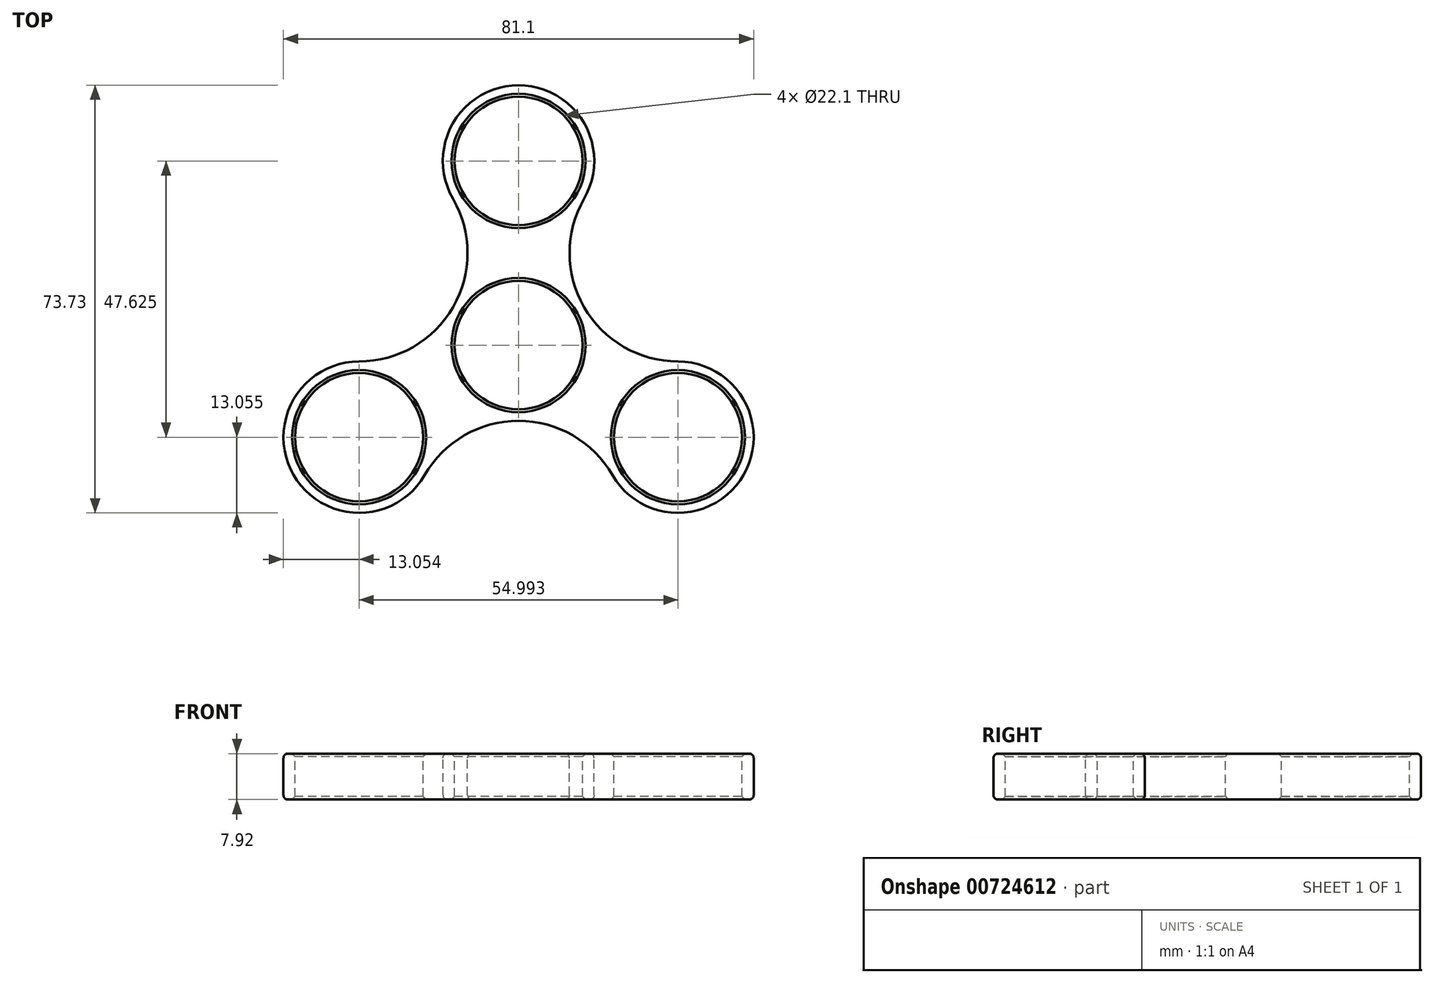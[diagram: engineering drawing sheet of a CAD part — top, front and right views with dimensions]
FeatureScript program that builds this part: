
annotation { "Feature Type Name" : "Feature", "Feature Type Description" : "" }
export const myFeature = defineFeature(function(context is Context, id is Id, definition is map)
    precondition{}
    {
        {
            var Q0;
            Q0=qCreatedBy(makeId("Top.planeOp"),FACE);
            var sketch = newSketch(context, id + "F0", { "sketchPlane" : qUnion([Q0])});
            skCircle(sketch, "E0", {"center": v(0, 0) * mm, "radius": 11.05 * mm});
            skCircle(sketch, "E1", {"center": v(0, 31.75) * mm, "radius": 11.05 * mm});
            skArc(sketch, "E2", {"start": v(11.3, 25.23) * mm, "mid": v(0, 44.8) * mm, "end": v(-11.3, 25.23) * mm});
            skCircle(sketch, "E3.1.0", {"center": v(-27.5, -15.87) * mm, "radius": 11.05 * mm});
            skArc(sketch, "E3.1.1", {"start": v(-27.5, -2.82) * mm, "mid": v(-38.8, -22.4) * mm, "end": v(-16.2, -22.4) * mm});
            skCircle(sketch, "E3.2.0", {"center": v(27.5, -15.88) * mm, "radius": 11.05 * mm});
            skArc(sketch, "E3.2.1", {"start": v(16.2, -22.4) * mm, "mid": v(38.8, -22.4) * mm, "end": v(27.5, -2.83) * mm});
            skArc(sketch, "E4", {"start": v(11.3, 25.22) * mm, "mid": v(11.3, 6.53) * mm, "end": v(27.5, -2.83) * mm});
            skArc(sketch, "E5.1.0", {"start": v(-27.5, -2.82) * mm, "mid": v(-11.3, 6.52) * mm, "end": v(-11.3, 25.22) * mm});
            skArc(sketch, "E5.2.0", {"start": v(16.2, -22.4) * mm, "mid": v(0, -13.05) * mm, "end": v(-16.2, -22.4) * mm});
            skSolve(sketch);
        }
        {
            var Q0;
            Q0 = qSketchRegion(id + "F0", true);
            extrude(context, id + "F1", {"entities" : qUnion([Q0]), "oppositeDirection" : true, "depth" : 7.92 * mm, "offsetDistance" : 25.4 * mm});
        }
        {
            var Q0;
            Q0=makeQuery(id+"F1.opExtrude","CAP_EDGE",EDGE,{"disambiguationData":[OSD([sQuery(id+"F0.wireOp",EDGE,"E3.2.0")])],"isStart":false});
            var Q1;
            Q1=makeQuery(id+"F1.opExtrude","CAP_EDGE",EDGE,{"disambiguationData":[OSD([sQuery(id+"F0.wireOp",EDGE,"E3.2.0")])],"isStart":true});
            var Q2;
            Q2=makeQuery(id+"F1.opExtrude","CAP_EDGE",EDGE,{"disambiguationData":[OSD([sQuery(id+"F0.wireOp",EDGE,"E3.1.0")])],"isStart":false});
            var Q3;
            Q3=makeQuery(id+"F1.opExtrude","CAP_EDGE",EDGE,{"disambiguationData":[OSD([sQuery(id+"F0.wireOp",EDGE,"E3.1.0")])],"isStart":true});
            var Q4;
            Q4=makeQuery(id+"F1.opExtrude","CAP_EDGE",EDGE,{"disambiguationData":[OSD([sQuery(id+"F0.wireOp",EDGE,"E0")])],"isStart":true});
            var Q5;
            Q5=makeQuery(id+"F1.opExtrude","CAP_EDGE",EDGE,{"disambiguationData":[OSD([sQuery(id+"F0.wireOp",EDGE,"E0")])],"isStart":false});
            var Q6;
            Q6=makeQuery(id+"F1.opExtrude","CAP_EDGE",EDGE,{"disambiguationData":[OSD([sQuery(id+"F0.wireOp",EDGE,"E1")])],"isStart":false});
            var Q7;
            Q7=makeQuery(id+"F1.opExtrude","CAP_EDGE",EDGE,{"disambiguationData":[OSD([sQuery(id+"F0.wireOp",EDGE,"E1")])],"isStart":true});
            chamfer(context, id + "F2", {"entities" : qUnion([Q0, Q1, Q2, Q3, Q4, Q5, Q6, Q7]), "width" : 0.5 * mm, "tangentPropagation" : true});
        }
        {
            var Q0;
            Q0=makeQuery(id+"F1.opExtrude","CAP_EDGE",EDGE,{"disambiguationData":[OSD([sQuery(id+"F0.wireOp",EDGE,"E5.1.0")])],"isStart":true});
            var Q1;
            Q1=makeQuery(id+"F1.opExtrude","CAP_EDGE",EDGE,{"disambiguationData":[OSD([sQuery(id+"F0.wireOp",EDGE,"E5.2.0")])],"isStart":false});
            fillet(context, id + "F3", {"entities" : qUnion([Q0, Q1]), "radius" : 0.76 * mm, "tangentPropagation" : true, "allowEdgeOverflow" : false});
        }
    });
